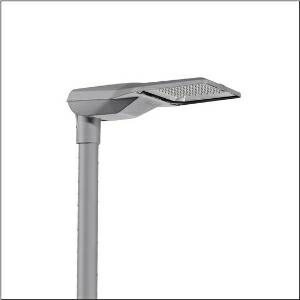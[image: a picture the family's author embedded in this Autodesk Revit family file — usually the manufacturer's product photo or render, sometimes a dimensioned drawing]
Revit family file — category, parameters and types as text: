
# Revit family: streetlight_sl_21_iq_midi___st0_5a_5xe3b41g08nb_d4f3
name_source: partatom
category: Lighting Fixtures
units: mm (PartAtom-declared; Revit-internal decimal feet)

## family parameters
Cut with Voids When Loaded = No
Host = Face
Light Source = No
Part Type = Normal
Room Calculation Point = No
Round Connector Dimension = Use Diameter
Shared = No

## types (1)
- --- (1 x LED, 24250 lm, 155.5 W, 4000K)
    Apparent Load = 155 VA
    CIE Flux Codes = 43 76 97 100 100
    Color Rendering = 70
    Color Temperature = 4000K
    Default Elevation = 1800 mm
    Description = Streetlight SL 21 iQ midi, mast luminaire, primary light control with lens, of PMMA, primary optical cover: cover, of toughened safety glass, transparent, light distribution: ST0.5a, light emission: direct distribution, primary light characteristic: asymmetric, installation type: post-top, side-entry, LED, High Power LED, rated luminous flux: 24.250lm, luminous efficacy: 156lm/W, light colour: 740, colour temperature: 4000K, control gear: iQ Street-Remote, control: Street-Remote, Auto-Match, Temp-Guard, Lumen-Switch, Night-Set, Smart-Wire, Light-Fading, Desk-Remote (wireless, voltage-free reading and setting of iQ features in the workshop via application-optimized NFC function/RFID function), optimised constant luminous flux control (CLO 2.0), pre-setting: linear dimming characteristic, mains connection: 230..240V, AC, 50/60Hz, start of lifetime: 156W, end of service life: 162W, reduction: 69W, luminaire housing, of diecast aluminium, powder-coated, SITECO metallic grey (DB 702S), corrosivity category C5 high according to DIN EN ISO 12944, please order mast flange separately, inclination adjustable: 0°, 5°, 10°, 15°, sealing non-destructively replaceable, multi-level sealing system, length: 644mm, width: 335mm, height: 110mm, mast flange for spigot size: 42mm (side-entry): 5XC10008XM4, 60/48mm (side-entry/post-top): 5XC10108XM2, 76/60mm (side-entry/post-top): 5XC10108XM1, mounting height: 4..8m, protection rating (complete): IP66, insulation class (complete): insulation class II (safety insulation), certification: CE, ENEC, ENEC+, VDE, impact resistance: IK10, permissible operating ambient temperature for outdoor applications: -40..+50°C, standard-compliant lighting for roads and squares, packaging unit: 1 piece

Light Distribution: ST0.5a
    Height = 111 mm
    Lamp = 1 x LED
    Lamp Light Flux = 24250 lm
    Lamp Power = 155.5 W
    Lamp count = 1
    Length = 644 mm
    Luminous efficacy = 156 lm/W
    Manufacturer = Siteco
    ModVariant = No
    Model = 5XE3B41G08NB
    Number of Poles = 1
    OnlyDefault = Yes
    Power Factor = 1
    Product Name = Streetlight SL 21 iQ midi | ST0.5a
    Product group = mast luminaire | pylon top
    ProductGroupID = 6100
    Protection Class = Protection class II
    Protection Degree = IP 66
    RLX_Detail_Level = 1
    RLX_Emergency_Light_Flux = 0 lm
    RLX_Emergency_Type = 0
    RLX_Emergency_Type_DB = No
    RlxData = <blob elided: 38389 chars, md5=245f237b>
    Socket = socket
    Standby Power = 0 W
    System Light Flux = 24250 lm
    System Power = 155 W
    Type Comments = factory setting: luminous flux: 100 % | dim-lin: 254 | 823 mA
    Type Image = l_1004298.jpg
    URL = http://relux.com
    VarID = @adj_170943
    Voltage = 0 V
    Weight = 0.00 kg
    Width = 336 mm

## geometry (parser evidence)
native form markers: Blend x4, Sweep x9
no freeform markers — native parametric forms only
